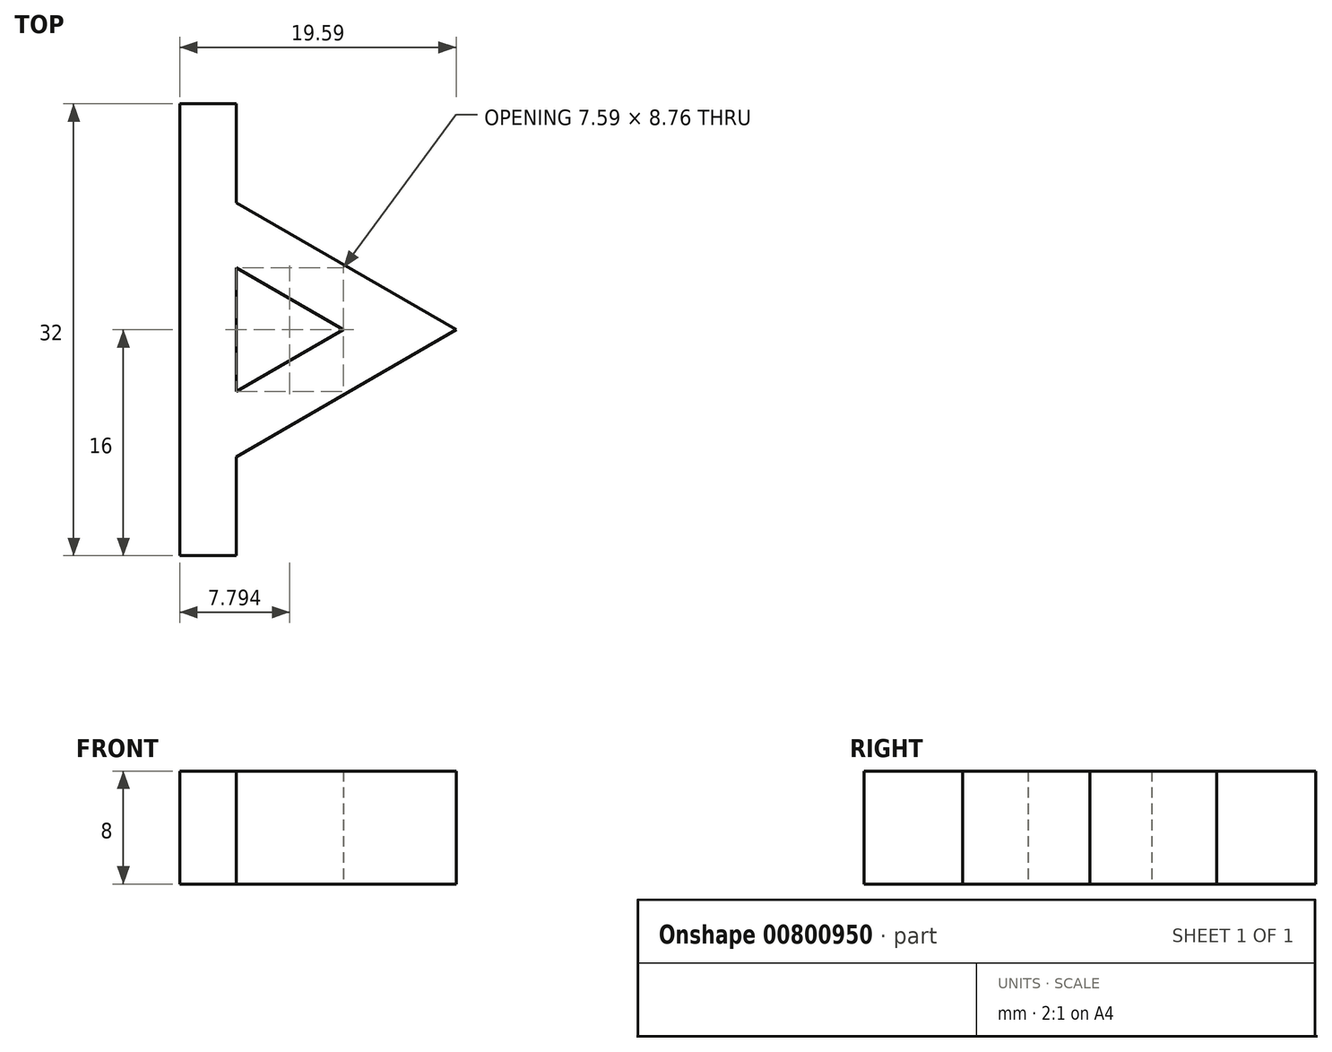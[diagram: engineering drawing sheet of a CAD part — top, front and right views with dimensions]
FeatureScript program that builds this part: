
annotation { "Feature Type Name" : "Feature", "Feature Type Description" : "" }
export const myFeature = defineFeature(function(context is Context, id is Id, definition is map)
    precondition{}
    {
        {
            var Q0;
            Q0=qCreatedBy(makeId("Top.planeOp"),FACE);
            var sketch = newSketch(context, id + "F0", { "sketchPlane" : qUnion([Q0])});
            skLineSegment(sketch, "E0", {"start": v(0, 0) * mm, "end": v(0, -32) * mm});
            skLineSegment(sketch, "E1", {"start": v(0, -32) * mm, "end": v(4, -32) * mm});
            skLineSegment(sketch, "E2", {"start": v(4, -32) * mm, "end": v(4, -25) * mm});
            skLineSegment(sketch, "E3", {"start": v(4, -25) * mm, "end": v(19.59, -16) * mm});
            skLineSegment(sketch, "E4", {"start": v(19.59, -16) * mm, "end": v(4, -7) * mm});
            skLineSegment(sketch, "E5", {"start": v(4, -7) * mm, "end": v(4, 0) * mm});
            skLineSegment(sketch, "E6", {"start": v(4, 0) * mm, "end": v(0, 0) * mm});
            skLineSegment(sketch, "E7", {"start": v(4, -11.62) * mm, "end": v(4, -20.38) * mm});
            skLineSegment(sketch, "E8", {"start": v(4, -20.38) * mm, "end": v(11.59, -16) * mm});
            skLineSegment(sketch, "E9", {"start": v(11.59, -16) * mm, "end": v(4, -11.62) * mm});
            skSolve(sketch);
        }
        {
            var Q0;
            Q0=makeQuery(id+"F0.imprint","IMPRINT",FACE,{"disambiguationData":[TD([[makeQuery(id+"F0.imprint","IMPRINT",EDGE,{"derivedFrom":sQuery(id+"F0.wireOp",EDGE,"E0")}),1.0]])]});
            extrude(context, id + "F1", {"entities" : qUnion([Q0]), "depth" : 8 * mm, "offsetDistance" : 25 * mm});
        }
    });
